# Revit family: Gira_011631
name_source: partatom
category: Electrical Fixtures
revit_build: Autodesk Revit 2017 (Build: 20160225_1515(x64)
units: mm (PartAtom-declared; Revit-internal decimal feet)

## family parameters
Always vertical = Yes
Cut with Voids When Loaded = No
Host = Wall
Maintain Annotation Orientation = No
OmniClass Number = 23.80.00.00
OmniClass Title = Electric Power and Lighting
Part Type = Normal
Room Calculation Point = No
Round Connector Dimension = Use Diameter
Shared = No

## types (1)
- Rock.ind.sw. off/2-way in.sp. WD surface-mounted grey
    Assembly arrangement = Basic element with complete housing
    BIM = https://media.live.bim.site und Tasten.rfa
    BIMSITE_PRODUCT_ID = ed81b6212588b44af35908d5c60bacdf791d7e3c
    Colour = Grey
    Connection type = Plug clamp
    Cost = 0 $
    Description = Rock.ind.sw.off 2-w in.sp. WT SM GY Rocker indicator switch 10 AX 250 V~ with inscription space Universal off 2-way switch grey Features: - With neon lamp element.,Notes : - Can also be connected with illumination.
    Function lighting = Illuminated (on)
    GTIN = 4010337116318
    HAN = 011631
    Halogen free = No
    HeinzeBIM = https://www.heinze.de
    Illumination = yes
    Label space/information surface = yes
    Manufacturer = Gira
    Material = Sonstige (*de-DE)
    Material quality = Sonstige (*de-DE)
    Method of operation = Rocker/button
    Nominal voltage [Volt] Number = 250
    Number of modules (module system) = 1
    Number of rockers = 1
    Push button switch = No
    Rated current [Ampere] = 10
    Suitable for degree of protection (IP) = IP66
    Surface protection = Sonstige (*de-DE)
    Type of fastening = Screw mounting
    Type of lighting = Glow lamp
    URL = https://www.gira.de
    Washing machine switch = No
    White = White
    Wiring system = Two-way switch
    With mounting plate = No

## geometry (parser evidence)
native form markers: Blend x2, Sweep x5
no freeform markers — native parametric forms only
